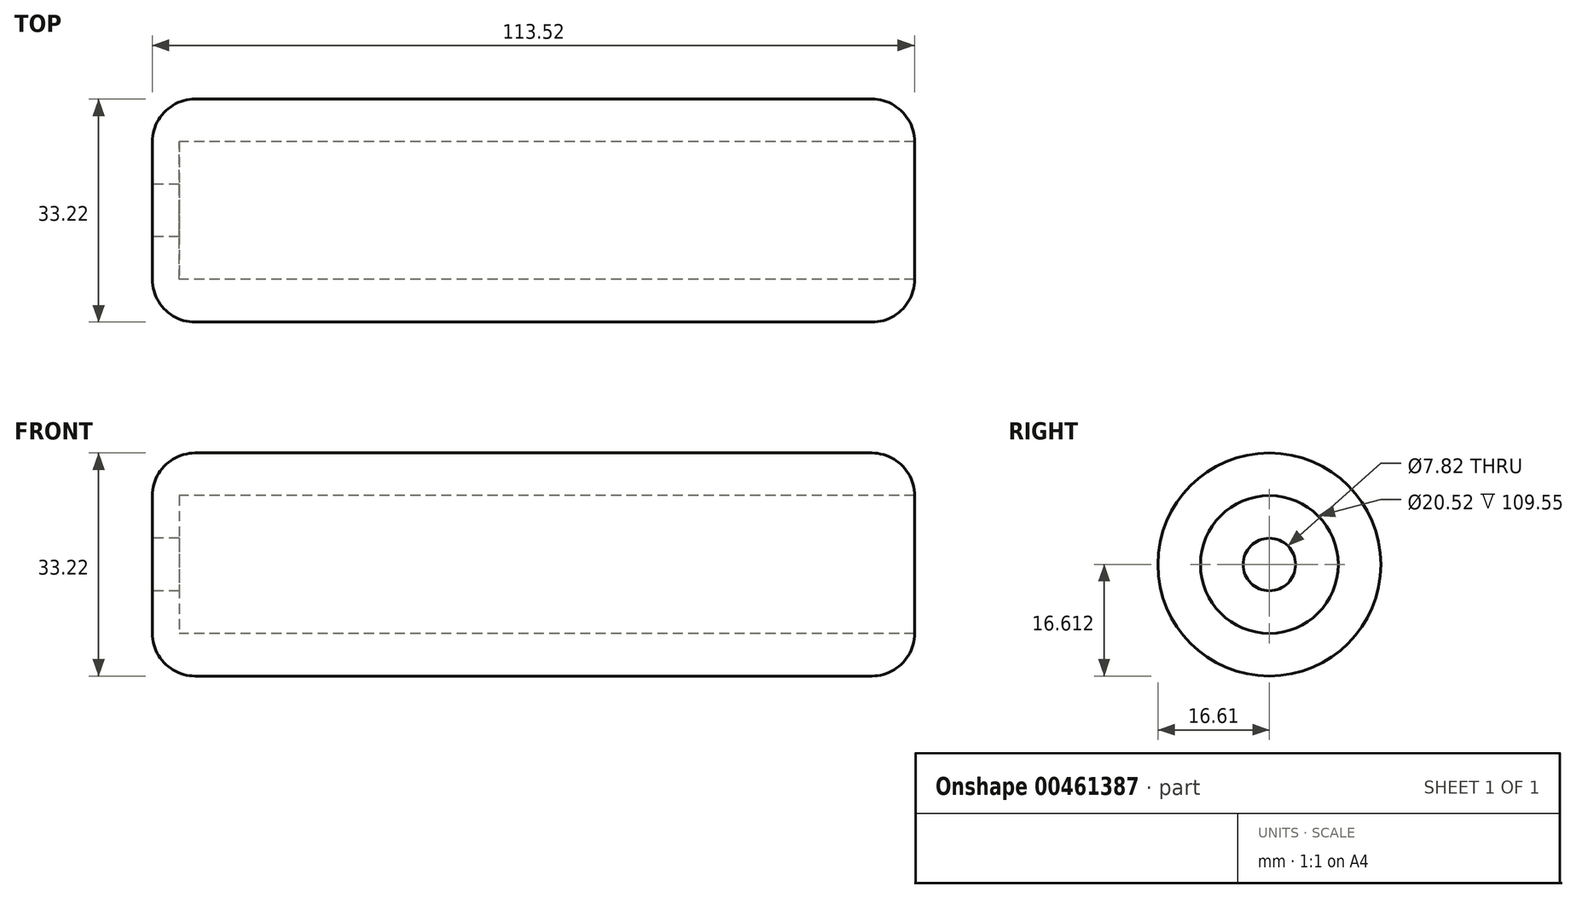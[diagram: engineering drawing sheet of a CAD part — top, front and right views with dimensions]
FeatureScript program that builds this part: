
annotation { "Feature Type Name" : "Feature", "Feature Type Description" : "" }
export const myFeature = defineFeature(function(context is Context, id is Id, definition is map)
    precondition{}
    {
        {
            var Q0;
            Q0=qCreatedBy(makeId("Front.planeOp"),FACE);
            var sketch = newSketch(context, id + "F0", { "sketchPlane" : qUnion([Q0])});
            skLineSegment(sketch, "E0", {"start": v(-68.27, 0) * mm, "end": v(45.25, 0) * mm});
            skLineSegment(sketch, "E1", {"start": v(38.9, 0) * mm, "end": v(-61.92, 0) * mm});
            skLineSegment(sketch, "E2", {"start": v(-68.27, 12.7) * mm, "end": v(-64.3, 12.7) * mm});
            skLineSegment(sketch, "E3", {"start": v(-64.3, 12.7) * mm, "end": v(-64.3, 6.35) * mm});
            skLineSegment(sketch, "E4", {"start": v(-64.3, 6.35) * mm, "end": v(45.25, 6.35) * mm});
            skLineSegment(sketch, "E5", {"start": v(45.25, 6.35) * mm, "end": v(45.25, 6.35) * mm});
            skLineSegment(sketch, "E6", {"start": v(-68.27, 12.7) * mm, "end": v(-68.27, 6.35) * mm});
            skLineSegment(sketch, "E7", {"start": v(-68.27, 16.61) * mm, "end": v(45.25, 16.61) * mm, "construction": true});
            skPoint(sketch, "E8.visualSharp", {"position": v(-68.27, 0) * mm});
            skArc(sketch, "E8.filletArc", {"start": v(-68.27, 6.35) * mm, "mid": v(-66.4, 1.86) * mm, "end": v(-61.92, 0) * mm});
            skPoint(sketch, "E9.visualSharp", {"position": v(45.25, 0) * mm});
            skArc(sketch, "E9.filletArc", {"start": v(38.9, 0) * mm, "mid": v(43.39, 1.86) * mm, "end": v(45.25, 6.35) * mm});
            skSolve(sketch);
        }
        {
            var Q0;
            Q0 = qSketchRegion(id + "F0", true);
            var Q1;
            Q1=sQuery(id+"F0.wireOp",EDGE,"E7");
            revolve(context, id + "F1", {"entities" : qUnion([Q0]), "axis" : qUnion([Q1]), "revolveType" : RevolveType.FULL});
        }
    });
